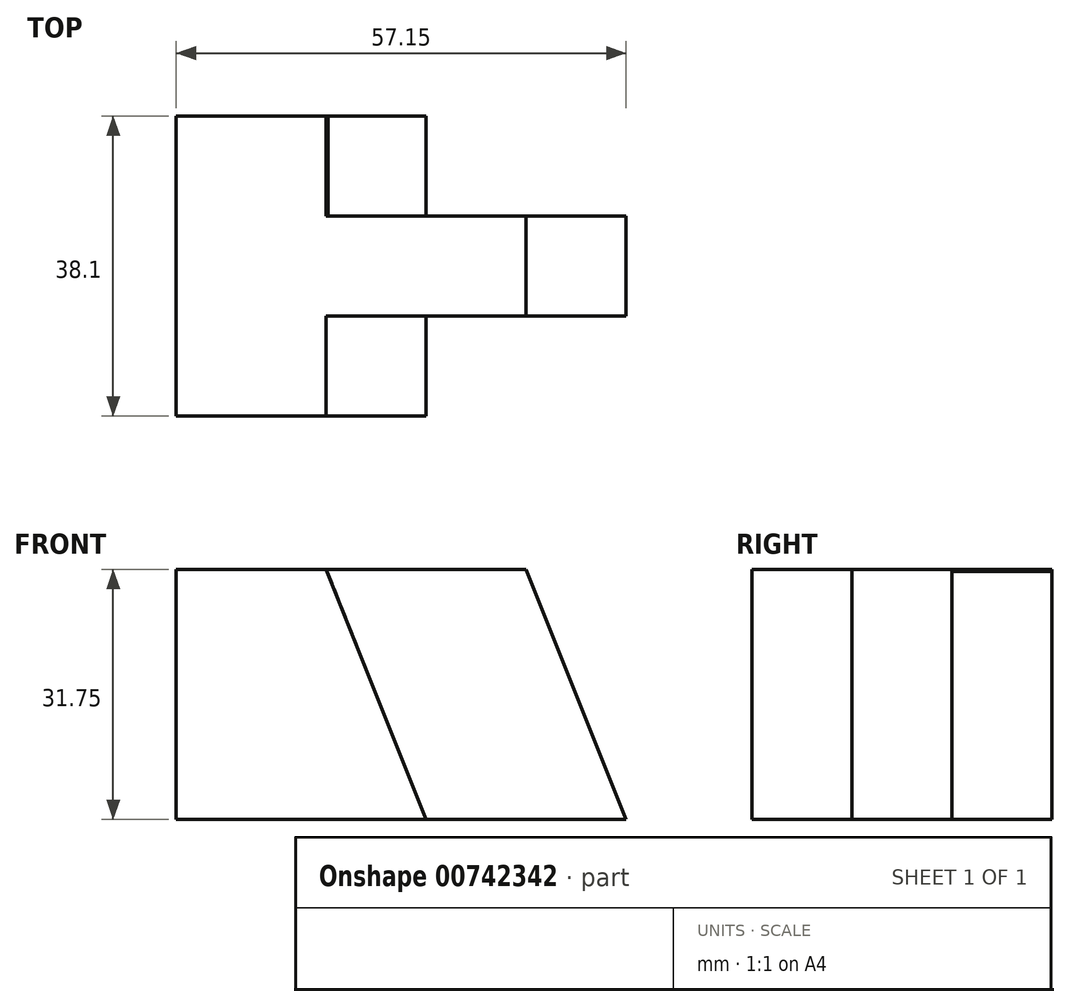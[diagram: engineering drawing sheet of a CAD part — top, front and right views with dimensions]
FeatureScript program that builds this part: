
annotation { "Feature Type Name" : "Feature", "Feature Type Description" : "" }
export const myFeature = defineFeature(function(context is Context, id is Id, definition is map)
    precondition{}
    {
        {
            var Q0;
            Q0=qCreatedBy(makeId("Front.planeOp"),FACE);
            var sketch = newSketch(context, id + "F0", { "sketchPlane" : qUnion([Q0])});
            skLineSegment(sketch, "E0", {"start": v(-57.15, 31.75) * mm, "end": v(-57.15, 0) * mm});
            skLineSegment(sketch, "E1", {"start": v(-57.15, 0) * mm, "end": v(0, 0) * mm});
            skLineSegment(sketch, "E2", {"start": v(0, 0) * mm, "end": v(0, 31.75) * mm});
            skLineSegment(sketch, "E3", {"start": v(0, 31.75) * mm, "end": v(-57.15, 31.75) * mm});
            skSolve(sketch);
        }
        {
            var Q0;
            Q0 = qSketchRegion(id + "F0", true);
            var Q1;
            Q1=makeQuery(id+"F0.imprint","IMPRINT",FACE,{"disambiguationData":[TD([[makeQuery(id+"F0.imprint","IMPRINT",EDGE,{"derivedFrom":sQuery(id+"F0.wireOp",EDGE,"E0")}),1.0]])]});
            extrude(context, id + "F1", {"entities" : qUnion([Q0, Q1]), "depth" : 38.1 * mm, "offsetDistance" : 25.4 * mm});
        }
        {
            var Q0;
            Q0=makeQuery(id+"F1.opExtrude","CAP_FACE",FACE,{"disambiguationData":[OSD([sQuery(id+"F0.wireOp",EDGE,"E0"),sQuery(id+"F0.wireOp",EDGE,"E1"),sQuery(id+"F0.wireOp",EDGE,"E2"),sQuery(id+"F0.wireOp",EDGE,"E3")])],"isStart":false});
            var sketch = newSketch(context, id + "F2", { "sketchPlane" : qUnion([Q0])});
            skLineSegment(sketch, "E4", {"start": v(-38.1, 31.75) * mm, "end": v(-25.4, 0) * mm});
            skSolve(sketch);
        }
        {
            var Q0;
            Q0 = qSketchRegion(id + "F2", true);
            var Q1;
            {var subQ0=sQuery(id+"F2.wireOp",EDGE,"E4");Q1=makeQuery(id+"F2.imprint","IMPRINT",FACE,{"disambiguationData":[TD([[makeQuery(id+"F2.imprint","IMPRINT",EDGE,{"derivedFrom":subQ0}),1.0]])]});}
            var Q2;
            Q2=makeQuery(id+"F1.opExtrude","CAP_FACE",FACE,{"disambiguationData":[OSD([sQuery(id+"F0.wireOp",EDGE,"E0"),sQuery(id+"F0.wireOp",EDGE,"E1"),sQuery(id+"F0.wireOp",EDGE,"E2"),sQuery(id+"F0.wireOp",EDGE,"E3")])],"isStart":true});
            extrude(context, id + "F3", {"entities" : qUnion([Q0, Q1, Q2]), "operationType" : NewBodyOperationType.REMOVE, "oppositeDirection" : true, "depth" : 12.7 * mm, "offsetDistance" : 25.4 * mm});
        }
        {
            var Q0;
            Q0=makeQuery(id+"F1.opExtrude","CAP_FACE",FACE,{"disambiguationData":[OSD([sQuery(id+"F0.wireOp",EDGE,"E0"),sQuery(id+"F0.wireOp",EDGE,"E1"),sQuery(id+"F0.wireOp",EDGE,"E2"),sQuery(id+"F0.wireOp",EDGE,"E3")])],"isStart":true});
            var sketch = newSketch(context, id + "F4", { "sketchPlane" : qUnion([Q0])});
            skLineSegment(sketch, "E5", {"start": v(38.1, 31.75) * mm, "end": v(0, 0) * mm});
            skSolve(sketch);
        }
        {
            var Q0;
            Q0 = qSketchRegion(id + "F4", true);
            var Q1;
            {var subQ0=sQuery(id+"F4.wireOp",EDGE,"E5");Q1=makeQuery(id+"F4.imprint","IMPRINT",FACE,{"disambiguationData":[TD([[makeQuery(id+"F4.imprint","IMPRINT",EDGE,{"derivedFrom":subQ0}),-1.0]])]});}
            extrude(context, id + "F5", {"entities" : qUnion([Q0, Q1]), "operationType" : NewBodyOperationType.ADD, "depth" : 12.7 * mm, "offsetDistance" : 25.4 * mm});
        }
        {
            var Q0;
            Q0=makeQuery(id+"F5.opExtrude","CAP_FACE",FACE,{"disambiguationData":[OSD([sQuery(id+"F0.wireOp",EDGE,"E2"),sQuery(id+"F0.wireOp",EDGE,"E3"),sQuery(id+"F4.wireOp",EDGE,"E5")])],"isStart":false});
            extrude(context, id + "F6", {"entities" : qUnion([Q0]), "operationType" : NewBodyOperationType.REMOVE, "oppositeDirection" : true, "depth" : 12.7 * mm, "offsetDistance" : 25.4 * mm});
        }
        {
            var Q0;
            {var subQ0=sQuery(id+"F0.wireOp",EDGE,"E3");var subQ1=sQuery(id+"F0.wireOp",EDGE,"E2");Q0=makeQuery(id+"F6.boolean.opBoolean","MERGE",FACE,{"derivedFrom":[makeQuery(id+"F1.opExtrude","CAP_FACE",FACE,{"disambiguationData":[OSD([sQuery(id+"F0.wireOp",EDGE,"E0"),sQuery(id+"F0.wireOp",EDGE,"E1"),subQ1,subQ0])],"isStart":true}),makeQuery(id+"F6.opExtrude","CAP_FACE",FACE,{"disambiguationData":[OSD([subQ1,subQ0,sQuery(id+"F4.wireOp",EDGE,"E5")])],"isStart":false})]});}
            var sketch = newSketch(context, id + "F7", { "sketchPlane" : qUnion([Q0])});
            skLineSegment(sketch, "E6", {"start": v(0, 0) * mm, "end": v(38.1, 31.75) * mm});
            skSolve(sketch);
        }
        {
            var Q0;
            {var subQ0=sQuery(id+"F7.wireOp",EDGE,"E6");Q0=makeQuery(id+"F7.imprint","IMPRINT",FACE,{"disambiguationData":[TD([[makeQuery(id+"F7.imprint","IMPRINT",EDGE,{"derivedFrom":subQ0}),-1.0]])]});}
            var sketch = newSketch(context, id + "F8", { "sketchPlane" : qUnion([Q0])});
            skLineSegment(sketch, "E7", {"start": v(25.4, 0) * mm, "end": v(38.1, 32.2) * mm});
            skSolve(sketch);
        }
        {
            var Q0;
            Q0 = qSketchRegion(id + "F8", true);
            var Q1;
            {var subQ0=sQuery(id+"F8.wireOp",EDGE,"E7");var subQ1=makeQuery(id+"F7.imprint","IMPRINT",EDGE,{"derivedFrom":makeQuery(id+"F1.opExtrude","CAP_EDGE",EDGE,{"disambiguationData":[OSD([sQuery(id+"F0.wireOp",EDGE,"E1")])],"isStart":true})});var subQ2=makeQuery(id+"F8.imprint","INTERSECT",VERTEX,{"derivedFrom":[subQ1,subQ0]});Q1=makeQuery(id+"F8.imprint","IMPRINT",FACE,{"disambiguationData":[TD([[makeQuery(id+"F8.imprint","IMPRINT",EDGE,{"disambiguationData":[TD([[subQ2,-1.0]])],"derivedFrom":subQ0}),1.0]])]});}
            var Q2;
            {var subQ0=sQuery(id+"F7.wireOp",EDGE,"E6");Q2=makeQuery(id+"F7.imprint","IMPRINT",FACE,{"disambiguationData":[TD([[makeQuery(id+"F7.imprint","IMPRINT",EDGE,{"derivedFrom":subQ0}),1.0]])]});}
            extrude(context, id + "F9", {"entities" : qUnion([Q0, Q1, Q2]), "operationType" : NewBodyOperationType.REMOVE, "oppositeDirection" : true, "depth" : 12.7 * mm, "offsetDistance" : 25.4 * mm});
        }
        {
            var Q0;
            Q0=makeQuery(id+"F3.boolean.opBoolean","COPY",FACE,{"derivedFrom":makeQuery(id+"F3.opExtrude","CAP_FACE",FACE,{"disambiguationData":[OSD([sQuery(id+"F0.wireOp",EDGE,"E1"),sQuery(id+"F0.wireOp",EDGE,"E2"),sQuery(id+"F0.wireOp",EDGE,"E3"),sQuery(id+"F2.wireOp",EDGE,"E4")])],"isStart":false})});
            var sketch = newSketch(context, id + "F10", { "sketchPlane" : qUnion([Q0])});
            skLineSegment(sketch, "E8", {"start": v(-12.7, 31.75) * mm, "end": v(0, 0) * mm});
            skSolve(sketch);
        }
        {
            var Q0;
            Q0 = qSketchRegion(id + "F10", true);
            var Q1;
            {var subQ0=sQuery(id+"F10.wireOp",EDGE,"E8");Q1=makeQuery(id+"F10.imprint","IMPRINT",FACE,{"disambiguationData":[TD([[makeQuery(id+"F10.imprint","IMPRINT",EDGE,{"derivedFrom":subQ0}),1.0]])]});}
            extrude(context, id + "F11", {"entities" : qUnion([Q0, Q1]), "operationType" : NewBodyOperationType.REMOVE, "endBound" : BoundingType.THROUGH_ALL, "oppositeDirection" : true, "depth" : 25.4 * mm, "offsetDistance" : 25.4 * mm});
        }
    });
